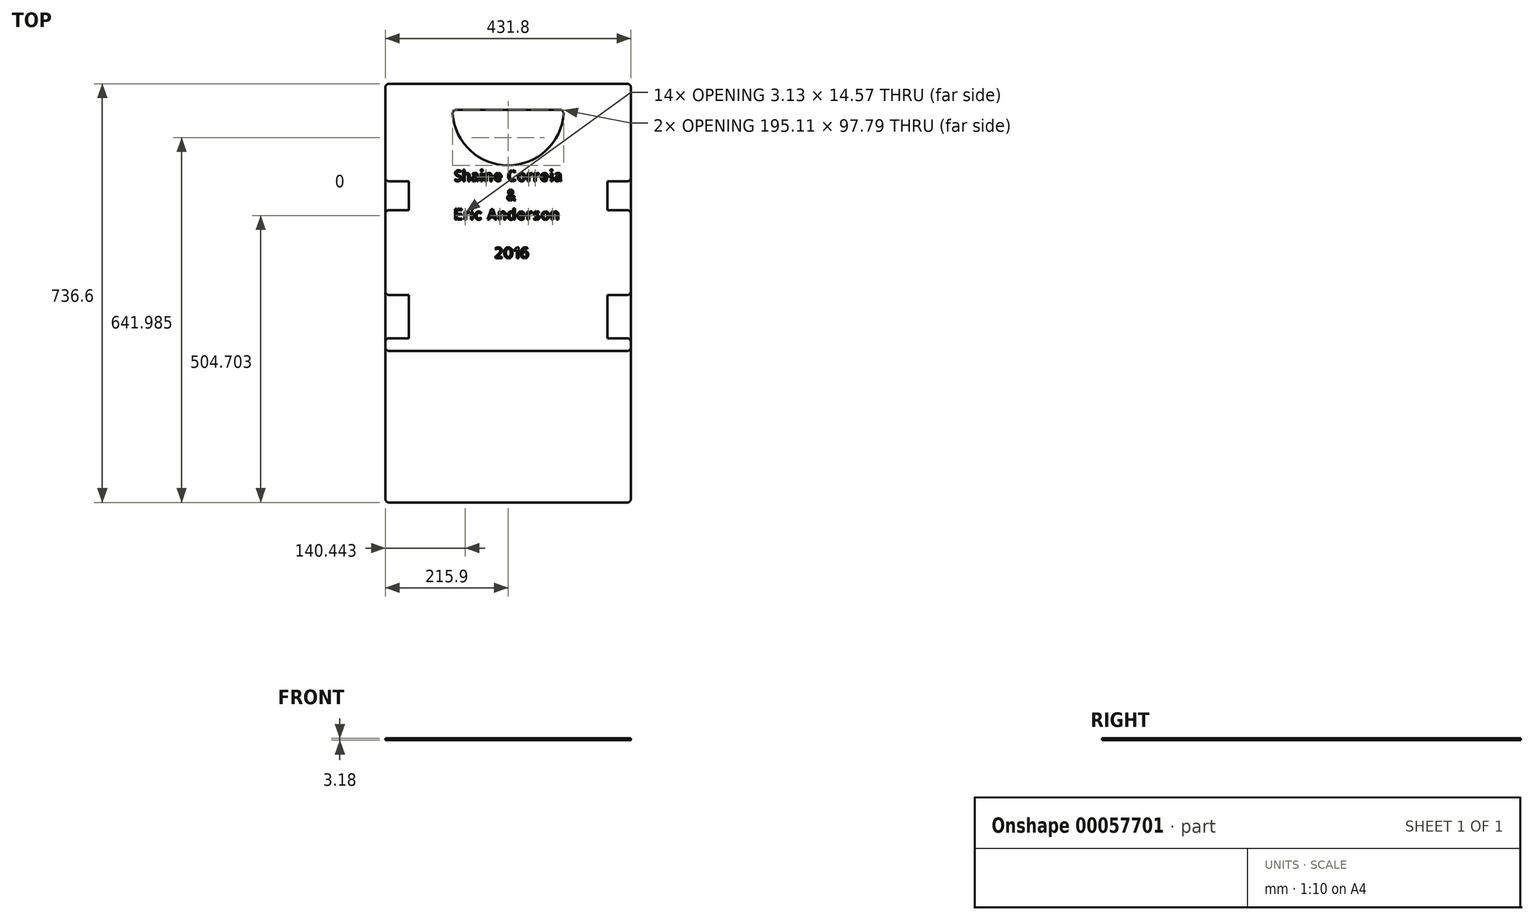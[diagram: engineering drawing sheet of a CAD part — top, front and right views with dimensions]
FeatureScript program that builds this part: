
annotation { "Feature Type Name" : "Feature", "Feature Type Description" : "" }
export const myFeature = defineFeature(function(context is Context, id is Id, definition is map)
    precondition{}
    {
        {
            var Q0;
            Q0=qCreatedBy(makeId("Top.planeOp"),FACE);
            var sketch = newSketch(context, id + "F0", { "sketchPlane" : qUnion([Q0])});
            skLineSegment(sketch, "E0.bottom", {"start": v(-215.9, -234.95) * mm, "end": v(215.9, -234.95) * mm});
            skLineSegment(sketch, "E0.top", {"start": v(-215.9, 234.95) * mm, "end": v(215.9, 234.95) * mm});
            skLineSegment(sketch, "E0.left", {"start": v(-215.9, -234.95) * mm, "end": v(-215.9, 234.95) * mm});
            skLineSegment(sketch, "E0.right", {"start": v(215.9, -234.95) * mm, "end": v(215.9, 234.95) * mm});
            skPoint(sketch, "E0.middle", {"position": v(0, 0) * mm});
            skSolve(sketch);
        }
        {
            var Q0;
            Q0=makeQuery(id+"F0.imprint","IMPRINT",FACE,{"disambiguationData":[TD([[makeQuery(id+"F0.imprint","IMPRINT",EDGE,{"derivedFrom":sQuery(id+"F0.wireOp",EDGE,"E0.bottom")}),1.0]])]});
            extrude(context, id + "F1", {"entities" : qUnion([Q0]), "depth" : 3.17 * mm});
        }
        {
            var Q0;
            Q0=qCreatedBy(makeId("Top.planeOp"),FACE);
            var sketch = newSketch(context, id + "F2", { "sketchPlane" : qUnion([Q0])});
            skLineSegment(sketch, "E1.0", {"start": v(-215.9, -234.95) * mm, "end": v(-215.9, -219.07) * mm});
            skLineSegment(sketch, "E2.0", {"start": v(215.9, -234.95) * mm, "end": v(215.9, -219.07) * mm});
            skLineSegment(sketch, "E3", {"start": v(-209.55, 234.95) * mm, "end": v(209.55, 234.95) * mm});
            skLineSegment(sketch, "E4.top", {"start": v(-209.55, -501.65) * mm, "end": v(209.55, -501.65) * mm});
            skLineSegment(sketch, "E4.left", {"start": v(-215.9, -234.95) * mm, "end": v(-215.9, -495.3) * mm});
            skLineSegment(sketch, "E4.right", {"start": v(215.9, -234.95) * mm, "end": v(215.9, -495.3) * mm});
            skLineSegment(sketch, "E5", {"start": v(0, 234.95) * mm, "end": v(0, -501.65) * mm, "construction": true});
            skLineSegment(sketch, "E6.bottom", {"start": v(209.55, -212.72) * mm, "end": v(174.63, -212.72) * mm});
            skLineSegment(sketch, "E6.top", {"start": v(209.55, -136.52) * mm, "end": v(174.62, -136.52) * mm});
            skLineSegment(sketch, "E6.right", {"start": v(174.63, -212.72) * mm, "end": v(174.63, -136.52) * mm});
            skLineSegment(sketch, "E7.bottom", {"start": v(209.55, 12.7) * mm, "end": v(174.62, 12.7) * mm});
            skLineSegment(sketch, "E7.top", {"start": v(209.55, 63.5) * mm, "end": v(174.62, 63.5) * mm});
            skLineSegment(sketch, "E7.right", {"start": v(174.62, 12.7) * mm, "end": v(174.62, 63.5) * mm});
            skLineSegment(sketch, "E8.MirrorCS", {"start": v(-209.55, -212.72) * mm, "end": v(-174.63, -212.72) * mm});
            skLineSegment(sketch, "E9.MirrorCS", {"start": v(-209.55, -136.52) * mm, "end": v(-174.62, -136.52) * mm});
            skLineSegment(sketch, "E10.MirrorCS", {"start": v(-174.62, -212.72) * mm, "end": v(-174.62, -136.53) * mm});
            skLineSegment(sketch, "E11.MirrorCS", {"start": v(-209.55, 12.7) * mm, "end": v(-174.63, 12.7) * mm});
            skLineSegment(sketch, "E12.MirrorCS", {"start": v(-209.55, 63.5) * mm, "end": v(-174.63, 63.5) * mm});
            skLineSegment(sketch, "E13.MirrorCS", {"start": v(-174.63, 12.7) * mm, "end": v(-174.63, 63.5) * mm});
            skPoint(sketch, "E14.visualSharp", {"position": v(-215.9, 234.95) * mm});
            skArc(sketch, "E14.filletArc", {"start": v(-209.55, 234.95) * mm, "mid": v(-214.04, 233.1) * mm, "end": v(-215.9, 228.6) * mm});
            skPoint(sketch, "E15.visualSharp", {"position": v(215.9, 234.95) * mm});
            skArc(sketch, "E15.filletArc", {"start": v(215.9, 228.6) * mm, "mid": v(214.04, 233.1) * mm, "end": v(209.55, 234.95) * mm});
            skPoint(sketch, "E16.visualSharp", {"position": v(215.9, -501.65) * mm});
            skArc(sketch, "E16.filletArc", {"start": v(209.55, -501.65) * mm, "mid": v(214.04, -499.8) * mm, "end": v(215.9, -495.3) * mm});
            skPoint(sketch, "E17.visualSharp", {"position": v(-215.9, -501.65) * mm});
            skArc(sketch, "E17.filletArc", {"start": v(-215.9, -495.3) * mm, "mid": v(-214.04, -499.8) * mm, "end": v(-209.55, -501.65) * mm});
            skLineSegment(sketch, "E18.trimOffspring", {"start": v(-215.9, 69.85) * mm, "end": v(-215.9, 228.6) * mm});
            skLineSegment(sketch, "E19.trimOffspring", {"start": v(-215.9, -130.17) * mm, "end": v(-215.9, 6.35) * mm});
            skLineSegment(sketch, "E20.trimOffspring", {"start": v(215.9, -130.17) * mm, "end": v(215.9, 6.35) * mm});
            skLineSegment(sketch, "E21.trimOffspring", {"start": v(215.9, 69.85) * mm, "end": v(215.9, 228.6) * mm});
            skPoint(sketch, "E22.visualSharp", {"position": v(-215.9, 63.5) * mm});
            skArc(sketch, "E22.filletArc", {"start": v(-215.9, 69.85) * mm, "mid": v(-214.04, 65.36) * mm, "end": v(-209.55, 63.5) * mm});
            skPoint(sketch, "E23.visualSharp", {"position": v(-215.9, 12.7) * mm});
            skArc(sketch, "E23.filletArc", {"start": v(-209.55, 12.7) * mm, "mid": v(-214.04, 10.84) * mm, "end": v(-215.9, 6.35) * mm});
            skPoint(sketch, "E24.visualSharp", {"position": v(-215.9, -136.52) * mm});
            skArc(sketch, "E24.filletArc", {"start": v(-215.9, -130.17) * mm, "mid": v(-214.04, -134.67) * mm, "end": v(-209.55, -136.52) * mm});
            skPoint(sketch, "E25.visualSharp", {"position": v(-215.9, -212.72) * mm});
            skArc(sketch, "E25.filletArc", {"start": v(-209.55, -212.73) * mm, "mid": v(-214.04, -214.58) * mm, "end": v(-215.9, -219.07) * mm});
            skPoint(sketch, "E26.visualSharp", {"position": v(215.9, -212.72) * mm});
            skArc(sketch, "E26.filletArc", {"start": v(215.9, -219.07) * mm, "mid": v(214.04, -214.58) * mm, "end": v(209.55, -212.72) * mm});
            skPoint(sketch, "E27.visualSharp", {"position": v(215.9, -136.52) * mm});
            skArc(sketch, "E27.filletArc", {"start": v(209.55, -136.52) * mm, "mid": v(214.04, -134.67) * mm, "end": v(215.9, -130.17) * mm});
            skPoint(sketch, "E28.visualSharp", {"position": v(215.9, 12.7) * mm});
            skArc(sketch, "E28.filletArc", {"start": v(215.9, 6.35) * mm, "mid": v(214.04, 10.84) * mm, "end": v(209.55, 12.7) * mm});
            skPoint(sketch, "E29.visualSharp", {"position": v(215.9, 63.5) * mm});
            skArc(sketch, "E29.filletArc", {"start": v(209.55, 63.5) * mm, "mid": v(214.04, 65.36) * mm, "end": v(215.9, 69.85) * mm});
            skSolve(sketch);
        }
        {
            var Q0;
            Q0=makeQuery(id+"F2.imprint","IMPRINT",FACE,{"disambiguationData":[TD([[makeQuery(id+"F2.imprint","IMPRINT",EDGE,{"derivedFrom":sQuery(id+"F2.wireOp",EDGE,"E1.0")}),-1.0]])]});
            extrude(context, id + "F3", {"entities" : qUnion([Q0]), "depth" : 3.17 * mm});
        }
        {
            var Q0;
            Q0=makeQuery(id+"F1.opExtrude","SWEPT_EDGE",EDGE,{"disambiguationData":[OSD([sQuery(id+"F0.wireOp",EDGE,"E0.bottom"),sQuery(id+"F0.wireOp",EDGE,"E0.right")])]});
            var Q1;
            Q1=makeQuery(id+"F1.opExtrude","SWEPT_EDGE",EDGE,{"disambiguationData":[OSD([sQuery(id+"F0.wireOp",EDGE,"E0.bottom"),sQuery(id+"F0.wireOp",EDGE,"E0.left")])]});
            var Q2;
            Q2=makeQuery(id+"F1.opExtrude","SWEPT_EDGE",EDGE,{"disambiguationData":[OSD([sQuery(id+"F0.wireOp",EDGE,"E0.top"),sQuery(id+"F0.wireOp",EDGE,"E0.right")])]});
            var Q3;
            Q3=makeQuery(id+"F1.opExtrude","SWEPT_EDGE",EDGE,{"disambiguationData":[OSD([sQuery(id+"F0.wireOp",EDGE,"E0.top"),sQuery(id+"F0.wireOp",EDGE,"E0.left")])]});
            fillet(context, id + "F4", {"entities" : qUnion([Q0, Q1, Q2, Q3]), "radius" : 6.35 * mm, "tangentPropagation" : true, "allowEdgeOverflow" : false});
        }
        {
            var Q0;
            Q0=makeQuery(id+"F3.opExtrude","CAP_FACE",FACE,{"disambiguationData":[OSD([sQuery(id+"F2.wireOp",EDGE,"E1.0"),sQuery(id+"F2.wireOp",EDGE,"E2.0"),sQuery(id+"F2.wireOp",EDGE,"E3"),sQuery(id+"F2.wireOp",EDGE,"E4.top"),sQuery(id+"F2.wireOp",EDGE,"E4.left"),sQuery(id+"F2.wireOp",EDGE,"E4.right"),sQuery(id+"F2.wireOp",EDGE,"E6.bottom"),sQuery(id+"F2.wireOp",EDGE,"E6.top"),sQuery(id+"F2.wireOp",EDGE,"E6.right"),sQuery(id+"F2.wireOp",EDGE,"E7.bottom"),sQuery(id+"F2.wireOp",EDGE,"E7.top"),sQuery(id+"F2.wireOp",EDGE,"E7.right"),sQuery(id+"F2.wireOp",EDGE,"E8.MirrorCS"),sQuery(id+"F2.wireOp",EDGE,"E9.MirrorCS"),sQuery(id+"F2.wireOp",EDGE,"E10.MirrorCS"),sQuery(id+"F2.wireOp",EDGE,"E11.MirrorCS"),sQuery(id+"F2.wireOp",EDGE,"E12.MirrorCS"),sQuery(id+"F2.wireOp",EDGE,"E13.MirrorCS"),sQuery(id+"F2.wireOp",EDGE,"E14.filletArc"),sQuery(id+"F2.wireOp",EDGE,"E15.filletArc"),sQuery(id+"F2.wireOp",EDGE,"E16.filletArc"),sQuery(id+"F2.wireOp",EDGE,"E17.filletArc"),sQuery(id+"F2.wireOp",EDGE,"E18.trimOffspring"),sQuery(id+"F2.wireOp",EDGE,"E19.trimOffspring"),sQuery(id+"F2.wireOp",EDGE,"E20.trimOffspring"),sQuery(id+"F2.wireOp",EDGE,"E21.trimOffspring"),sQuery(id+"F2.wireOp",EDGE,"E22.filletArc"),sQuery(id+"F2.wireOp",EDGE,"E23.filletArc"),sQuery(id+"F2.wireOp",EDGE,"E24.filletArc"),sQuery(id+"F2.wireOp",EDGE,"E25.filletArc"),sQuery(id+"F2.wireOp",EDGE,"E26.filletArc"),sQuery(id+"F2.wireOp",EDGE,"E27.filletArc"),sQuery(id+"F2.wireOp",EDGE,"E28.filletArc"),sQuery(id+"F2.wireOp",EDGE,"E29.filletArc")])],"isStart":false});
            var sketch = newSketch(context, id + "F5", { "sketchPlane" : qUnion([Q0])});
            skLineSegment(sketch, "E30", {"start": v(0, 234.95) * mm, "end": v(0, -501.65) * mm, "construction": true});
            skArc(sketch, "E31", {"start": v(-97.55, 182.44) * mm, "mid": v(0, 91.44) * mm, "end": v(97.55, 182.44) * mm});
            skLineSegment(sketch, "E32", {"start": v(-91.22, 189.23) * mm, "end": v(91.22, 189.23) * mm});
            skPoint(sketch, "E33.visualSharp", {"position": v(97.8, 189.23) * mm});
            skArc(sketch, "E33.filletArc", {"start": v(97.55, 182.44) * mm, "mid": v(95.86, 187.21) * mm, "end": v(91.22, 189.23) * mm});
            skPoint(sketch, "E34.visualSharp", {"position": v(-97.8, 189.23) * mm});
            skArc(sketch, "E34.filletArc", {"start": v(-91.22, 189.23) * mm, "mid": v(-95.86, 187.21) * mm, "end": v(-97.55, 182.44) * mm});
            skSolve(sketch);
        }
        {
            var Q0;
            Q0=makeQuery(id+"F5.imprint","IMPRINT",FACE,{"disambiguationData":[TD([[makeQuery(id+"F5.imprint","IMPRINT",EDGE,{"derivedFrom":sQuery(id+"F5.wireOp",EDGE,"E31")}),1.0]])]});
            extrude(context, id + "F6", {"entities" : qUnion([Q0]), "operationType" : NewBodyOperationType.REMOVE, "endBound" : BoundingType.THROUGH_ALL, "oppositeDirection" : true, "depth" : 25.4 * mm});
        }
        {
            var Q0;
            Q0=makeQuery(id+"F1.opExtrude","CAP_FACE",FACE,{"disambiguationData":[OSD([sQuery(id+"F0.wireOp",EDGE,"E0.bottom"),sQuery(id+"F0.wireOp",EDGE,"E0.top"),sQuery(id+"F0.wireOp",EDGE,"E0.left"),sQuery(id+"F0.wireOp",EDGE,"E0.right")])],"isStart":false});
            var sketch = newSketch(context, id + "F7", { "sketchPlane" : qUnion([Q0])});
            skText(sketch, "E35", { "text": "Shaine Correia \n             & \nEric Anderson\n\n          2016", "fontName": "AllertaStencil-Regular.ttf"});
            skLineSegment(sketch, "E36", {"start": v(0, 0) * mm, "end": v(0, 234.95) * mm, "construction": true});
            const initialGuessF7  = {"E35": [-0.09547, 0.0635, 1, 0, 0.01905]};
            skSetInitialGuess(sketch, initialGuessF7);
            skSolve(sketch);
        }
        {
            var Q0;
            Q0 = qSketchRegion(id + "F7", true);
            extrude(context, id + "F8", {"entities" : qUnion([Q0]), "operationType" : NewBodyOperationType.REMOVE, "endBound" : BoundingType.THROUGH_ALL, "oppositeDirection" : true, "depth" : 25.4 * mm});
        }
    });
